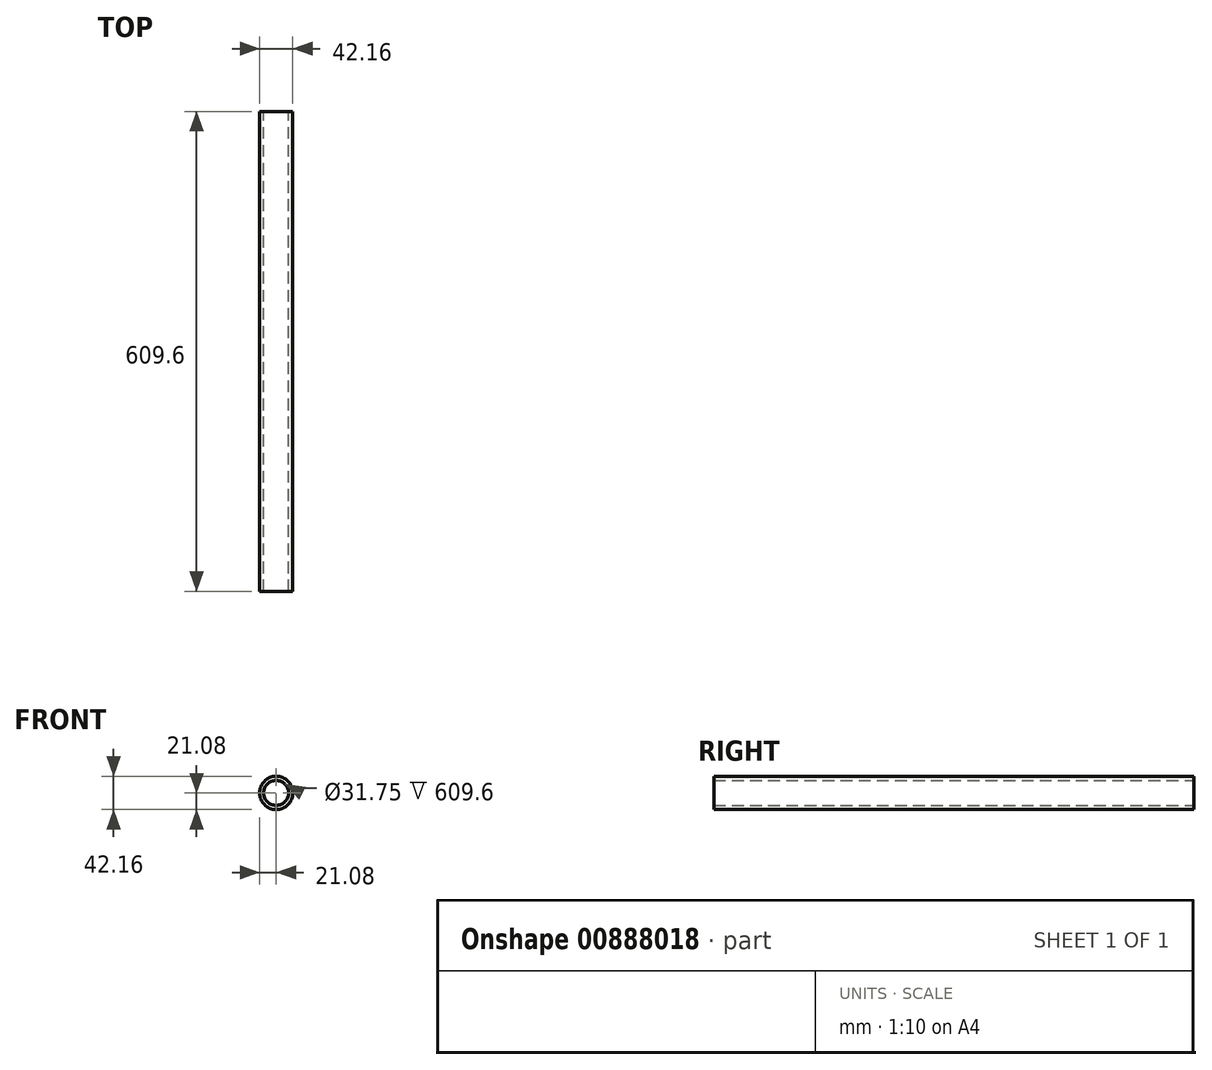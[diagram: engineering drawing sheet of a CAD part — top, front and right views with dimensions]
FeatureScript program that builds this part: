
annotation { "Feature Type Name" : "Feature", "Feature Type Description" : "" }
export const myFeature = defineFeature(function(context is Context, id is Id, definition is map)
    precondition{}
    {
        {
            var Q0;
            Q0=qCreatedBy(makeId("Front.planeOp"),FACE);
            var sketch = newSketch(context, id + "F0", { "sketchPlane" : qUnion([Q0])});
            skCircle(sketch, "E0", {"center": v(0, 0) * mm, "radius": 15.88 * mm});
            skCircle(sketch, "E1", {"center": v(0, 0) * mm, "radius": 21.08 * mm});
            skSolve(sketch);
        }
        {
            var Q0;
            Q0=makeQuery(id+"F0.imprint","IMPRINT",FACE,{"disambiguationData":[TD([[makeQuery(id+"F0.imprint","IMPRINT",EDGE,{"derivedFrom":sQuery(id+"F0.wireOp",EDGE,"E0")}),-1.0]])]});
            extrude(context, id + "F1", {"entities" : qUnion([Q0]), "depth" : 609.6 * mm, "offsetDistance" : 25.4 * mm});
        }
    });
